# Revit family: JOMA_444
name_source: partatom
category: Structural Connections
revit_build: Autodesk Revit 2017 (Build: 20190508_0315(x64)
units: mm (PartAtom-declared; Revit-internal decimal feet)

## family parameters
Cut with Voids When Loaded = No
Enable cutting in views = Yes
Host = Face
Material for Model Behavior = Other
Shared = No

## types (3) — shared parameters
Default Elevation = 1000 mm  [stored 3.28084 ft]
Länk joma dimensioneringsverktyg = http://www.joma.se
Material = Varmförzinkad stålplåt

## per-type parameters (varying)
| type | Beslag 4444001 | Beslag 4444002 | Beslag 4444003 | Vikt (Kg) | l |
| 4444001 | Yes | No | No | 0,325 | 100 mm  [stored 0.328084 ft] |
| 4444002 | No | Yes | No | 0,41 | 150 mm |
| 4444003 | No | No | Yes | 0,664 | 285 mm  [stored 0.935039 ft] |

note: [stored X ft] marks values corroborated as IEEE doubles in the binary element streams (Revit-internal decimal feet)

## geometry (parser evidence)
native form markers: Sweep x3
no freeform markers — native parametric forms only
